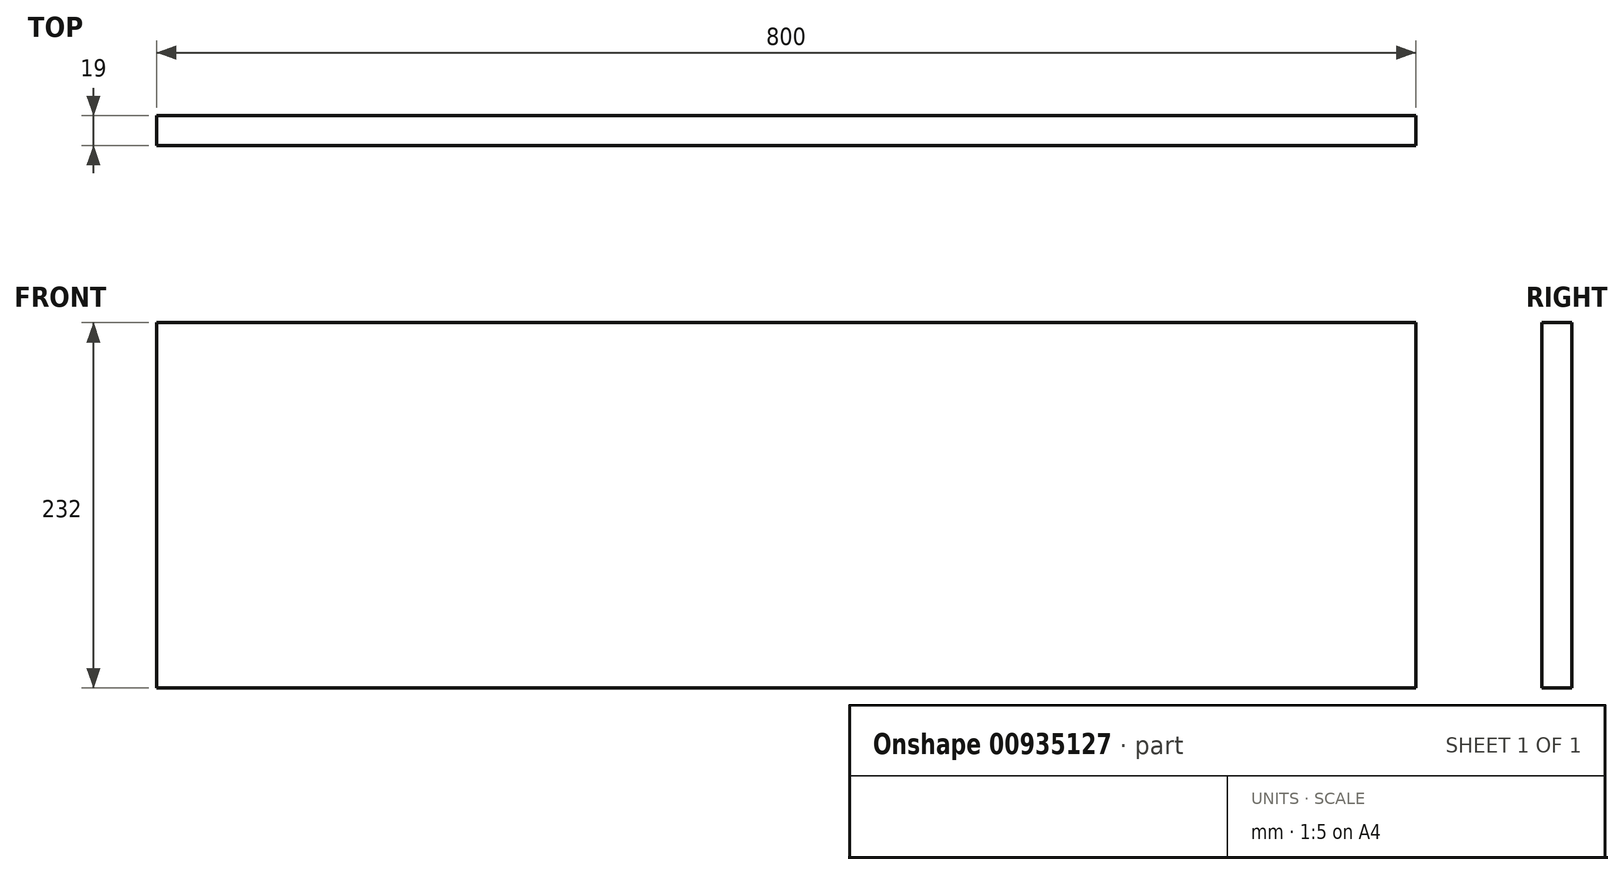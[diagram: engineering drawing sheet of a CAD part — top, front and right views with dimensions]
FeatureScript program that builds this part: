
annotation { "Feature Type Name" : "Feature", "Feature Type Description" : "" }
export const myFeature = defineFeature(function(context is Context, id is Id, definition is map)
    precondition{}
    {
        {
            var Q0;
            Q0=qCreatedBy(makeId("Front.planeOp"),FACE);
            var sketch = newSketch(context, id + "F0", { "sketchPlane" : qUnion([Q0])});
            skLineSegment(sketch, "E0.bottom", {"start": v(0, 0) * mm, "end": v(800, 0) * mm});
            skLineSegment(sketch, "E0.top", {"start": v(0, 232) * mm, "end": v(800, 232) * mm});
            skLineSegment(sketch, "E0.left", {"start": v(0, 0) * mm, "end": v(0, 232) * mm});
            skLineSegment(sketch, "E0.right", {"start": v(800, 0) * mm, "end": v(800, 232) * mm});
            skSolve(sketch);
        }
        {
            var Q0;
            Q0=makeQuery(id+"F0.imprint","IMPRINT",FACE,{"disambiguationData":[TD([[makeQuery(id+"F0.imprint","IMPRINT",EDGE,{"derivedFrom":sQuery(id+"F0.wireOp",EDGE,"E0.bottom")}),1.0]])]});
            extrude(context, id + "F1", {"entities" : qUnion([Q0]), "depth" : 19 * mm, "offsetDistance" : 25 * mm});
        }
    });
